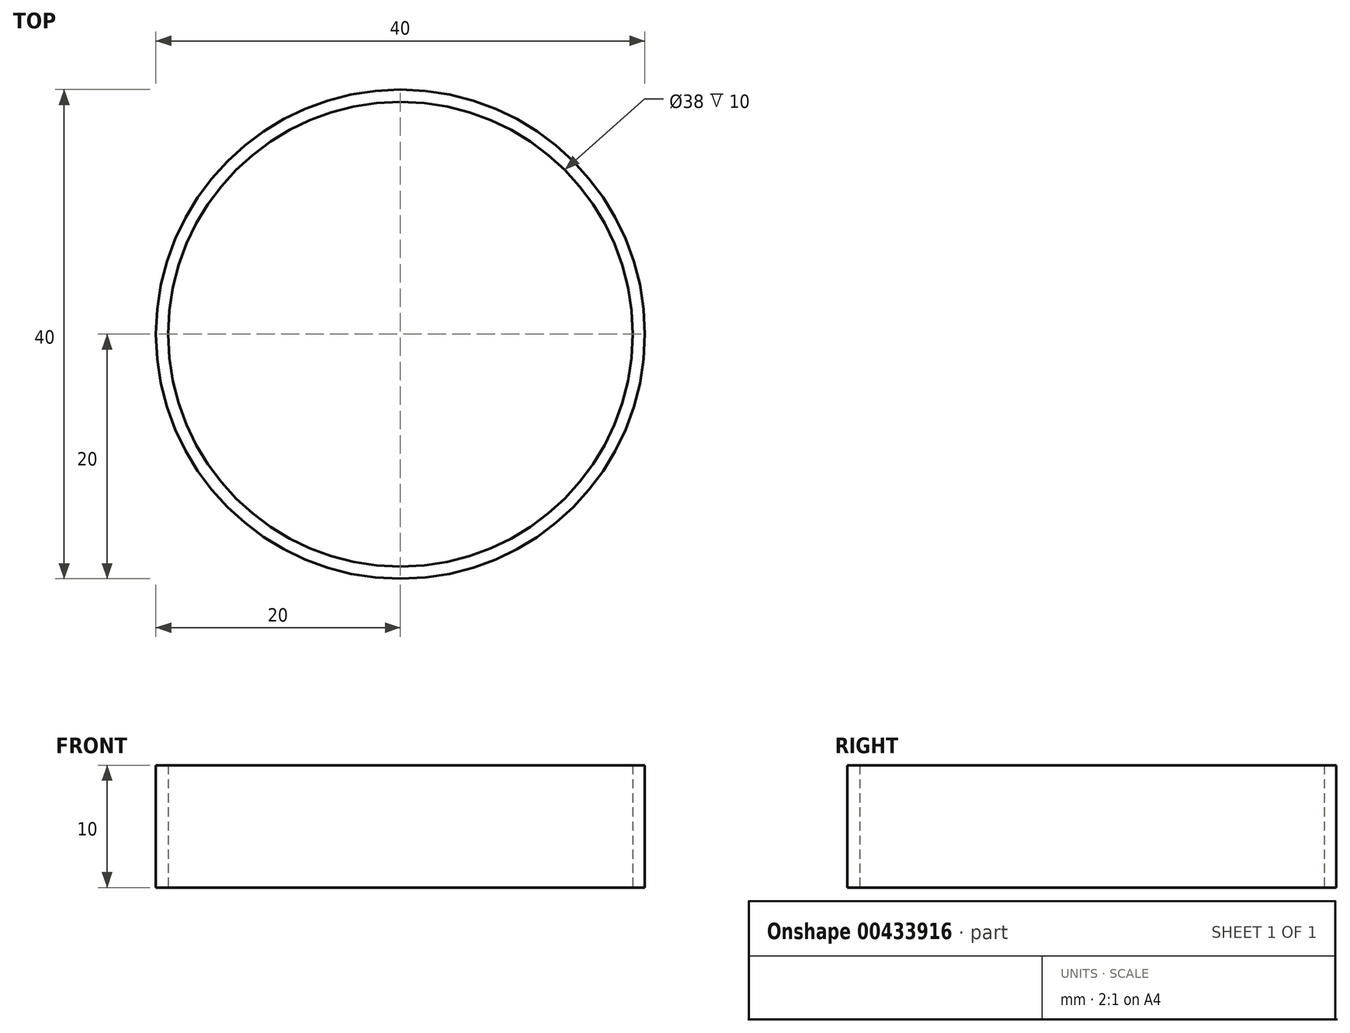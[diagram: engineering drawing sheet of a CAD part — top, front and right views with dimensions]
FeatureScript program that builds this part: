
annotation { "Feature Type Name" : "Feature", "Feature Type Description" : "" }
export const myFeature = defineFeature(function(context is Context, id is Id, definition is map)
    precondition{}
    {
        {
            var Q0;
            Q0=qCreatedBy(makeId("Top.planeOp"),FACE);
            var sketch = newSketch(context, id + "F0", { "sketchPlane" : qUnion([Q0])});
            skCircle(sketch, "E0", {"center": v(0, 0) * mm, "radius": 20 * mm});
            skCircle(sketch, "E1", {"center": v(0, 0) * mm, "radius": 19 * mm});
            skSolve(sketch);
        }
        {
            var Q0;
            Q0=makeQuery(id+"F0.imprint","IMPRINT",FACE,{"disambiguationData":[TD([[makeQuery(id+"F0.imprint","IMPRINT",EDGE,{"derivedFrom":sQuery(id+"F0.wireOp",EDGE,"E0")}),1.0]])]});
            extrude(context, id + "F1", {"entities" : qUnion([Q0]), "depth" : 10 * mm});
        }
    });
